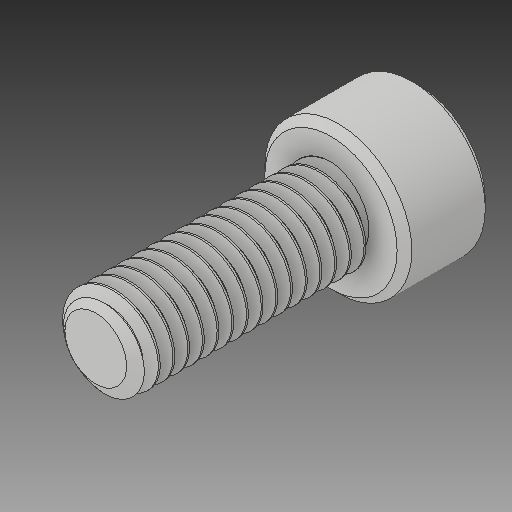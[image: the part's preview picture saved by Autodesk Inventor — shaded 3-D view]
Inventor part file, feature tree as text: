
AUTODESK INVENTOR PART (.ipt)
format: ipt  version: 2019.4 (Build 234330000, 330)  size: 716,288 bytes
history: native  units: in
note: dims shown in document units (in); Inventor stores cm internally (conversion verified against a paired STEP export)
features: chamfer x1
ambient origin geometry x8: Origin, YZ Plane, XZ Plane, XY Plane, X Axis, Y Axis, Z Axis, Center Point
bodies: Solid1 (feature_tree)
feature tree (1):
  chamfer  "Chamfer1"  [1 undecoded]
note: 1 required parameter value undecoded (feature->parameter linkage not recoverable at this tier; creation-order binding heuristic only, values carry confidence <= 0.55)
